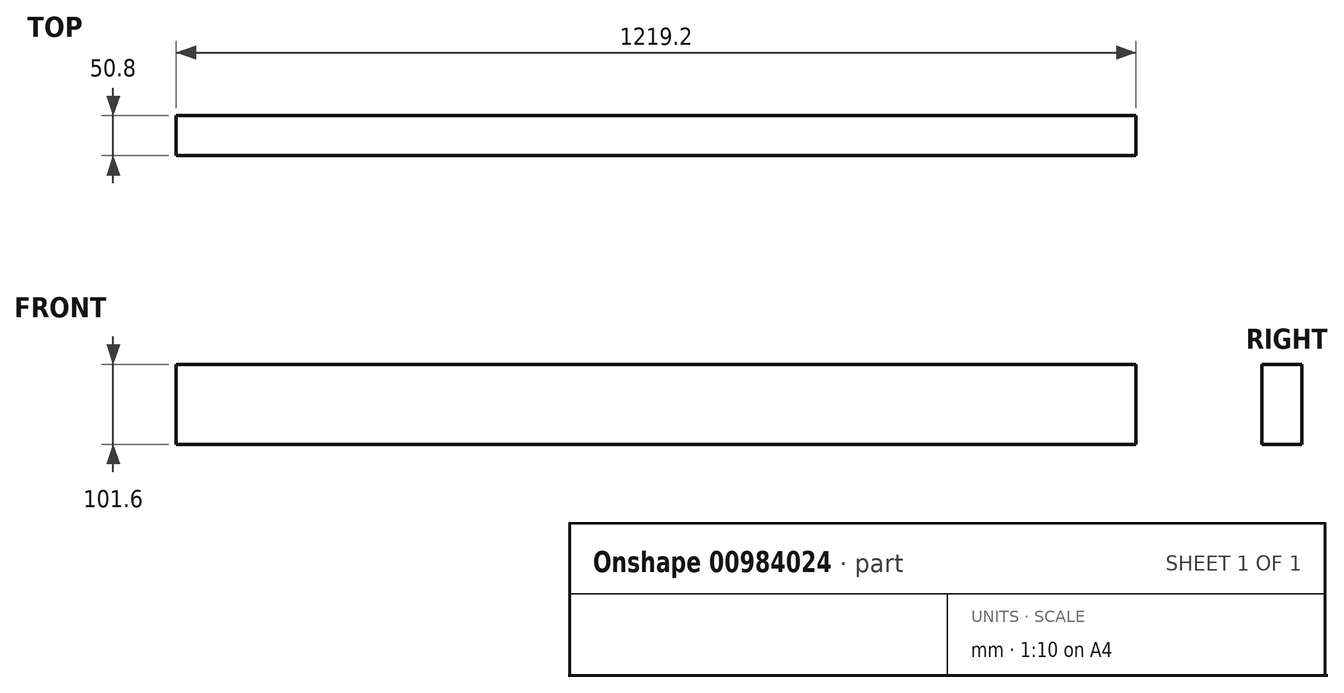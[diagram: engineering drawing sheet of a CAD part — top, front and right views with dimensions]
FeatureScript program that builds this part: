
annotation { "Feature Type Name" : "Feature", "Feature Type Description" : "" }
export const myFeature = defineFeature(function(context is Context, id is Id, definition is map)
    precondition{}
    {
        {
            var Q0;
            Q0=qCreatedBy(makeId("Right.planeOp"),FACE);
            var sketch = newSketch(context, id + "F0", { "sketchPlane" : qUnion([Q0])});
            skLineSegment(sketch, "E0.bottom", {"start": v(-25.4, 50.8) * mm, "end": v(25.4, 50.8) * mm});
            skLineSegment(sketch, "E0.top", {"start": v(-25.4, -50.8) * mm, "end": v(25.4, -50.8) * mm});
            skLineSegment(sketch, "E0.left", {"start": v(-25.4, 50.8) * mm, "end": v(-25.4, -50.8) * mm});
            skLineSegment(sketch, "E0.right", {"start": v(25.4, 50.8) * mm, "end": v(25.4, -50.8) * mm});
            skPoint(sketch, "E0.middle", {"position": v(0, 0) * mm});
            skSolve(sketch);
        }
        {
            var Q0;
            Q0 = qSketchRegion(id + "F0", true);
            extrude(context, id + "F1", {"entities" : qUnion([Q0]), "depth" : 1219.2 * mm, "offsetDistance" : 25.4 * mm});
        }
    });
